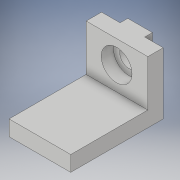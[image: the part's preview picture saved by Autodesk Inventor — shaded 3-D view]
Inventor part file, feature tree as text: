
AUTODESK INVENTOR PART (.ipt)
format: ipt  version: 2019 (Build 230136000, 136)  size: 126,976 bytes
history: native  units: in
note: dims shown in document units (in); Inventor stores cm internally (conversion verified against a paired STEP export)
features: sketch x3, extrude x2, projected_geometry x2, hole x1
ambient origin geometry x8: Origin, YZ Plane, XZ Plane, XY Plane, X Axis, Y Axis, Z Axis, Center Point
bodies: Solid1 (feature_tree)
feature tree (8):
  extrude  "Extrusion1"  Depth=0.5in
  extrude  "Extrusion2"  Depth=0.75in
  hole  "Hole3"  [1 undecoded]
  sketch  "Sketch1"  dims[d0=0.125in d1=0.5in]
  sketch  "Sketch4"  dims[d4=0.125in d5=0.75in]
  projected_geometry  "Projected Loop3"
  sketch  "Sketch5"  dims[d6=0.5in d7=0.0in d22=0.2in d23=0.5in d24=0.15in d25=0.0625in d26=0.0in d27=0.15in d28=0.75in d29=0.25in d30=0.1in d31=0.5635in d32=1.0in d33=0.8108in]
  projected_geometry  "Projected Loop4"
note: 1 required parameter value undecoded (feature->parameter linkage not recoverable at this tier; creation-order binding heuristic only, values carry confidence <= 0.55)
